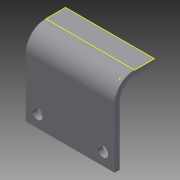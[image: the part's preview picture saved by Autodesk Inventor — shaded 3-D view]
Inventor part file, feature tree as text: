
AUTODESK INVENTOR PART (.ipt)
format: ipt  version: 2013 (Build 170138000, 138)  size: 117,760 bytes
history: native  units: in
note: dims shown in document units (in); Inventor stores cm internally (conversion verified against a paired STEP export)
features: sketch x6, sheet_metal_op x4, other x2
ambient origin geometry x8: Origin, YZ Plane, XZ Plane, XY Plane, X Axis, Y Axis, Z Axis, Center Point
bodies: Solid1 (feature_tree)
feature tree (12):
  sheet_metal_op  "Face1"
  sheet_metal_op  "Flange1"
  sketch  "Sketch3"  dims[d3=0.295in]
  sketch  "Sketch4"  dims[d4=1.181in]
  sketch  "Sketch5"  dims[d5=0.295in]
  sketch  "Sketch6"  dims[d6=0.26in d7=0.26in d8=0.125in d9=0.125in d10=0.0625in d11=0.25in d12=0.125in d13=1.0in d14=90.0deg d15=0.375in d16=0.5in d17=0.125in d18=0.125in]
  sketch  "Sketch1"  dims[d1=2.244in]
  other  "Plate1"
  sketch  "Sketch2"  dims[d2=1.5in]
  other  "Plate2"
  sheet_metal_op  "Bend1"
  sheet_metal_op  "Corner1"
